# Revit family: rstadvancedsamplefamily
name_source: partatom
category: Structural Columns
units: mm (PartAtom-declared; Revit-internal decimal feet)

## family parameters
Always export as geometry = No
Beam cutback in plan = From bounding box
Cut with Voids When Loaded = No
Display in Hidden Views = Edges Hidden by Other Members
Material for Model Behavior = Precast Concrete
OmniClass Number = 23.25.30.11.14.11
OmniClass Title = Columns
Section Shape = Not Defined
Shared = No
Show family pre-cut in plan views = No

## types (8) — shared parameters
Chamfer = 25 mm  [stored 0.082021 ft]
Corbel Depth East = 200 mm  [stored 0.656168 ft]
Corbel Depth North = 200 mm  [stored 0.656168 ft]
Corbel Depth South = 200 mm  [stored 0.656168 ft]
Corbel Depth West = 200 mm  [stored 0.656168 ft]
Corbel East 3 = No
Corbel East 4 = No
Corbel Height East = 400 mm  [stored 1.31234 ft]
Corbel Height North = 400 mm  [stored 1.31234 ft]
Corbel Height South = 400 mm  [stored 1.31234 ft]
Corbel Height West = 400 mm  [stored 1.31234 ft]
Corbel North 1 = Yes
Corbel North 4 = No
Corbel Width East = 150 mm
Corbel Width North = 150 mm
Corbel Width South = 150 mm
Corbel Width West = 150 mm

## per-type parameters (varying)
- 300x300-2 Levels: Corbel East 1=Yes; Corbel East 2=Yes; Corbel North 2=No; Corbel North 3=No; Corbel South 1=Yes; Corbel South 2=Yes; Corbel South 3=No; Corbel South 4=No; Corbel West 1=No; Corbel West 2=No; Corbel West 3=No; Corbel West 4=No; East Corbel Type=Rectangular Corbel; East Corbels Number=2; East Corbels Number 1=2; North Corbel Type=Sloped Corbel; North Corbels Number=1; North Corbels Number 1=1; South Corbel Type=Rectangular Corbel; South Corbels Number=2; South Corbels Number 1=2; West Corbel Type=Rectangular Corbel; West Corbels Number=0; West Corbels Number 1=0; b=300 mm  [stored 0.984252 ft]; h=300 mm  [stored 0.984252 ft]
- 450x450-2 Levels: Assembly Code=B10; Corbel East 1=No; Corbel East 2=No; Corbel North 2=Yes; Corbel North 3=No; Corbel South 1=No; Corbel South 2=No; Corbel South 3=No; Corbel South 4=No; Corbel West 1=Yes; Corbel West 2=Yes; Corbel West 3=No; Corbel West 4=No; East Corbel Type=Sloped Corbel; East Corbels Number=0; East Corbels Number 1=0; North Corbel Type=Rectangular Corbel; North Corbels Number=2; North Corbels Number 1=2; South Corbel Type=Rectangular Corbel; South Corbels Number=0; South Corbels Number 1=0; West Corbel Type=Sloped Corbel; West Corbels Number=2; West Corbels Number 1=2; b=450 mm  [stored 1.47638 ft]; h=450 mm  [stored 1.47638 ft]
- 300x300-4 Levels: Assembly Code=B10; Corbel East 1=No; Corbel East 2=No; Corbel North 2=Yes; Corbel North 3=Yes; Corbel South 1=Yes; Corbel South 2=Yes; Corbel South 3=Yes; Corbel South 4=Yes; Corbel West 1=Yes; Corbel West 2=No; Corbel West 3=No; Corbel West 4=No; East Corbel Type=Sloped Corbel; East Corbels Number=0; East Corbels Number 1=0; North Corbel Type=Sloped Corbel; North Corbels Number=3; North Corbels Number 1=3; South Corbel Type=Sloped Corbel; South Corbels Number=4; South Corbels Number 1=4; West Corbel Type=Sloped Corbel; West Corbels Number=1; West Corbels Number 1=1; b=300 mm  [stored 0.984252 ft]; h=300 mm  [stored 0.984252 ft]
- 300x300-3 Levels: Assembly Code=B10; Corbel East 1=No; Corbel East 2=No; Corbel North 2=Yes; Corbel North 3=No; Corbel South 1=No; Corbel South 2=No; Corbel South 3=No; Corbel South 4=No; Corbel West 1=Yes; Corbel West 2=Yes; Corbel West 3=Yes; Corbel West 4=No; East Corbel Type=Sloped Corbel; East Corbels Number=0; East Corbels Number 1=0; North Corbel Type=Sloped Corbel; North Corbels Number=2; North Corbels Number 1=2; South Corbel Type=Rectangular Corbel; South Corbels Number=0; South Corbels Number 1=0; West Corbel Type=Rectangular Corbel; West Corbels Number=3; West Corbels Number 1=3; b=300 mm  [stored 0.984252 ft]; h=300 mm  [stored 0.984252 ft]
- 450x450-4 Levels: Assembly Code=B10; Corbel East 1=Yes; Corbel East 2=Yes; Corbel North 2=No; Corbel North 3=No; Corbel South 1=No; Corbel South 2=No; Corbel South 3=No; Corbel South 4=No; Corbel West 1=Yes; Corbel West 2=Yes; Corbel West 3=Yes; Corbel West 4=Yes; East Corbel Type=Sloped Corbel; East Corbels Number=2; East Corbels Number 1=2; North Corbel Type=Rectangular Corbel; North Corbels Number=1; North Corbels Number 1=1; South Corbel Type=Rectangular Corbel; South Corbels Number=0; South Corbels Number 1=0; West Corbel Type=Sloped Corbel; West Corbels Number=4; West Corbels Number 1=4; b=450 mm  [stored 1.47638 ft]; h=450 mm  [stored 1.47638 ft]
- 450x450-3 Levels: Assembly Code=B10; Corbel East 1=Yes; Corbel East 2=Yes; Corbel North 2=No; Corbel North 3=No; Corbel South 1=Yes; Corbel South 2=Yes; Corbel South 3=Yes; Corbel South 4=No; Corbel West 1=No; Corbel West 2=No; Corbel West 3=No; Corbel West 4=No; East Corbel Type=Sloped Corbel; East Corbels Number=2; East Corbels Number 1=2; North Corbel Type=Sloped Corbel; North Corbels Number=1; North Corbels Number 1=1; South Corbel Type=Rectangular Corbel; South Corbels Number=3; South Corbels Number 1=3; West Corbel Type=Rectangular Corbel; West Corbels Number=0; West Corbels Number 1=0; b=450 mm  [stored 1.47638 ft]; h=450 mm  [stored 1.47638 ft]
- 300x300-1 Level: Assembly Code=B10; Corbel East 1=Yes; Corbel East 2=No; Corbel North 2=No; Corbel North 3=No; Corbel South 1=Yes; Corbel South 2=No; Corbel South 3=No; Corbel South 4=No; Corbel West 1=No; Corbel West 2=No; Corbel West 3=No; Corbel West 4=No; East Corbel Type=Sloped Corbel; East Corbels Number=1; East Corbels Number 1=1; North Corbel Type=Sloped Corbel; North Corbels Number=1; North Corbels Number 1=1; South Corbel Type=Sloped Corbel; South Corbels Number=1; South Corbels Number 1=1; West Corbel Type=Rectangular Corbel; West Corbels Number=0; West Corbels Number 1=0; b=300 mm  [stored 0.984252 ft]; h=300 mm  [stored 0.984252 ft]
- 450x450-1 Level: Assembly Code=B10; Corbel East 1=Yes; Corbel East 2=No; Corbel North 2=No; Corbel North 3=No; Corbel South 1=No; Corbel South 2=No; Corbel South 3=No; Corbel South 4=No; Corbel West 1=Yes; Corbel West 2=No; Corbel West 3=No; Corbel West 4=No; East Corbel Type=Sloped Corbel; East Corbels Number=1; East Corbels Number 1=1; North Corbel Type=Rectangular Corbel; North Corbels Number=1; North Corbels Number 1=1; South Corbel Type=Rectangular Corbel; South Corbels Number=0; South Corbels Number 1=0; West Corbel Type=Sloped Corbel; West Corbels Number=1; West Corbels Number 1=1; b=450 mm  [stored 1.47638 ft]; h=450 mm  [stored 1.47638 ft]

note: [stored X ft] marks values corroborated as IEEE doubles in the binary element streams (Revit-internal decimal feet)

## geometry (parser evidence)
native form markers: Sweep x6
no freeform markers — native parametric forms only
